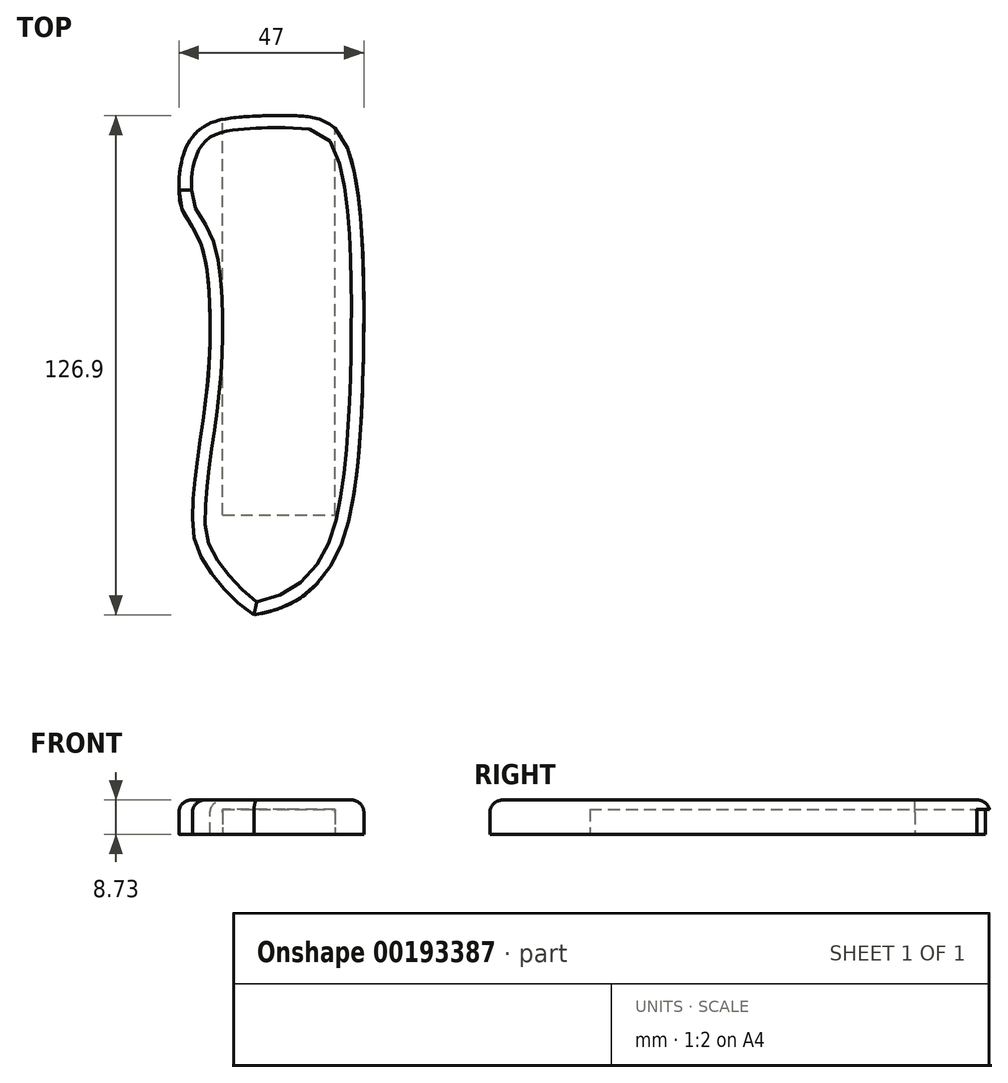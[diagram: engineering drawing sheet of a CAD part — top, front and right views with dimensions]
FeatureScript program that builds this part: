
annotation { "Feature Type Name" : "Feature", "Feature Type Description" : "" }
export const myFeature = defineFeature(function(context is Context, id is Id, definition is map)
    precondition{}
    {
        {
            var Q0;
            Q0=qCreatedBy(makeId("Top.planeOp"),FACE);
            var sketch = newSketch(context, id + "F0", { "sketchPlane" : qUnion([Q0])});
            skPoint(sketch, "E0.middle", {"position": v(0, 0) * mm});
            skPoint(sketch, "E1", {"position": v(-3.21, -50.8) * mm});
            skFitSpline(sketch, "E2", {"points": [v(-22.26, 57.15) * mm, v(-17.37, 45.2) * mm, v(-14.33, 23.81) * mm, v(-15.7, 1.92) * mm, v(-18.78, -27.76) * mm, v(-15.59, -37.83) * mm, v(-3.21, -50.8) * mm], "startDerivative": vector(0, -136.07) * mm, "endDerivative": vector(114.07, -78.4) * mm});
            skFitSpline(sketch, "E3", {"points": [v(4.7, 76.2) * mm, v(20.5, 67.98) * mm, v(24.64, 17.56) * mm, v(20.16, -29.54) * mm, v(12.69, -43) * mm, v(-3.21, -50.8) * mm], "startDerivative": vector(184.27, 2.28) * mm, "endDerivative": vector(-156.33, -28.06) * mm});
            skFitSpline(sketch, "E4", {"points": [v(-22.26, 57.15) * mm, v(-17.55, 72.08) * mm, v(-6.5, 75.82) * mm, v(4.7, 76.2) * mm], "startDerivative": vector(-1.74, 49.97) * mm, "endDerivative": vector(34.11, 0.26) * mm});
            skSolve(sketch);
        }
        {
            var Q0;
            Q0 = qSketchRegion(id + "F0", true);
            extrude(context, id + "F1", {"entities" : qUnion([Q0]), "depth" : 8.73 * mm});
        }
        {
            var Q0;
            Q0=makeQuery(id+"F1.opExtrude","CAP_FACE",FACE,{"disambiguationData":[OSD([sQuery(id+"F0.wireOp",EDGE,"cfad175f-5df1-4238-a212-687723bf9a46"),sQuery(id+"F0.wireOp",EDGE,"a22437ff-b6d7-45b8-94a2-b93b02e63303.trimOffspring"),sQuery(id+"F0.wireOp",EDGE,"YW74m88l-YdF0-uJPx-sHid-teXK335I2kme"),sQuery(id+"F0.wireOp",EDGE,"E2"),sQuery(id+"F0.wireOp",EDGE,"014a7305-8275-4df8-ac81-cba376bb9b54.trimOffspring"),sQuery(id+"F0.wireOp",EDGE,"34d715c5-a372-4039-8854-132d3a662aac")])],"isStart":false});
            fillet(context, id + "F2", {"entities" : qUnion([Q0]), "radius" : 3.17 * mm, "tangentPropagation" : true, "allowEdgeOverflow" : false});
        }
        {
            var Q0;
            Q0=makeQuery(id+"F1.opExtrude","CAP_FACE",FACE,{"disambiguationData":[OSD([sQuery(id+"F0.wireOp",EDGE,"cfad175f-5df1-4238-a212-687723bf9a46"),sQuery(id+"F0.wireOp",EDGE,"a22437ff-b6d7-45b8-94a2-b93b02e63303.trimOffspring"),sQuery(id+"F0.wireOp",EDGE,"YW74m88l-YdF0-uJPx-sHid-teXK335I2kme"),sQuery(id+"F0.wireOp",EDGE,"E2"),sQuery(id+"F0.wireOp",EDGE,"014a7305-8275-4df8-ac81-cba376bb9b54.trimOffspring"),sQuery(id+"F0.wireOp",EDGE,"34d715c5-a372-4039-8854-132d3a662aac")])],"isStart":true});
            var sketch = newSketch(context, id + "F3", { "sketchPlane" : qUnion([Q0])});
            skPoint(sketch, "E5", {"position": v(-108.07, 647.23) * mm});
            skPoint(sketch, "E6", {"position": v(95.4, 647.23) * mm});
            skPoint(sketch, "E7", {"position": v(4.7, -76.2) * mm});
            skPoint(sketch, "E8", {"position": v(-11.14, 25.4) * mm});
            skLineSegment(sketch, "E9.bottom", {"start": v(-11.14, 25.4) * mm, "end": v(17.44, 25.4) * mm});
            skLineSegment(sketch, "E9.top", {"start": v(-11.14, -101.6) * mm, "end": v(17.44, -101.6) * mm});
            skLineSegment(sketch, "E9.left", {"start": v(-11.14, 25.4) * mm, "end": v(-11.14, -101.6) * mm});
            skLineSegment(sketch, "E9.right", {"start": v(17.44, 25.4) * mm, "end": v(17.44, -101.6) * mm});
            skSolve(sketch);
        }
        {
            var Q0;
            Q0 = qSketchRegion(id + "F3", true);
            extrude(context, id + "F4", {"entities" : qUnion([Q0]), "operationType" : NewBodyOperationType.REMOVE, "oppositeDirection" : true, "depth" : 6.35 * mm});
        }
    });
